# Revit family: sh-4105
name_source: partatom
category: Lighting Fixtures
revit_build: Autodesk Revit 2017 (Build: 20160225_1515(x64)
units: mm (PartAtom-declared; Revit-internal decimal feet)

## family parameters
Always vertical = Yes
Cut with Voids When Loaded = No
Host = Wall
Light Source = No
OmniClass Number = 23.80.70.00
OmniClass Title = Lighting
Part Type = Normal
Room Calculation Point = No
Round Connector Dimension = Use Diameter
Shared = Yes

## types (2) — shared parameters
Body Material = Aluminum
Color Rendering (CRI) = 80
Color Temperature = 3000K
Flicker = Free Flicker
Height = 18.1 cm
IP = 54
Lamp = LED
Manufacturer = SHOA
Model = SH-4105
Type medule = SMD
URL = https://www.shoaco.com
Voltage/Frequency = 230 V Ac/50HZ
Website = www.shoaco.com
Width = 16.7 cm
consumption current = 0 A
instalation = Wall Mounted
wattage. = 6 W
zero-valued in all types: Cost

## per-type parameters (varying)
| type | Body Color |
| SH-4105(white body-3000K-LED) | white |
| SH-4105(Gray body-3000K-LED) | Gray |

## geometry (parser evidence)
native form markers: Sweep x4
no freeform markers — native parametric forms only
